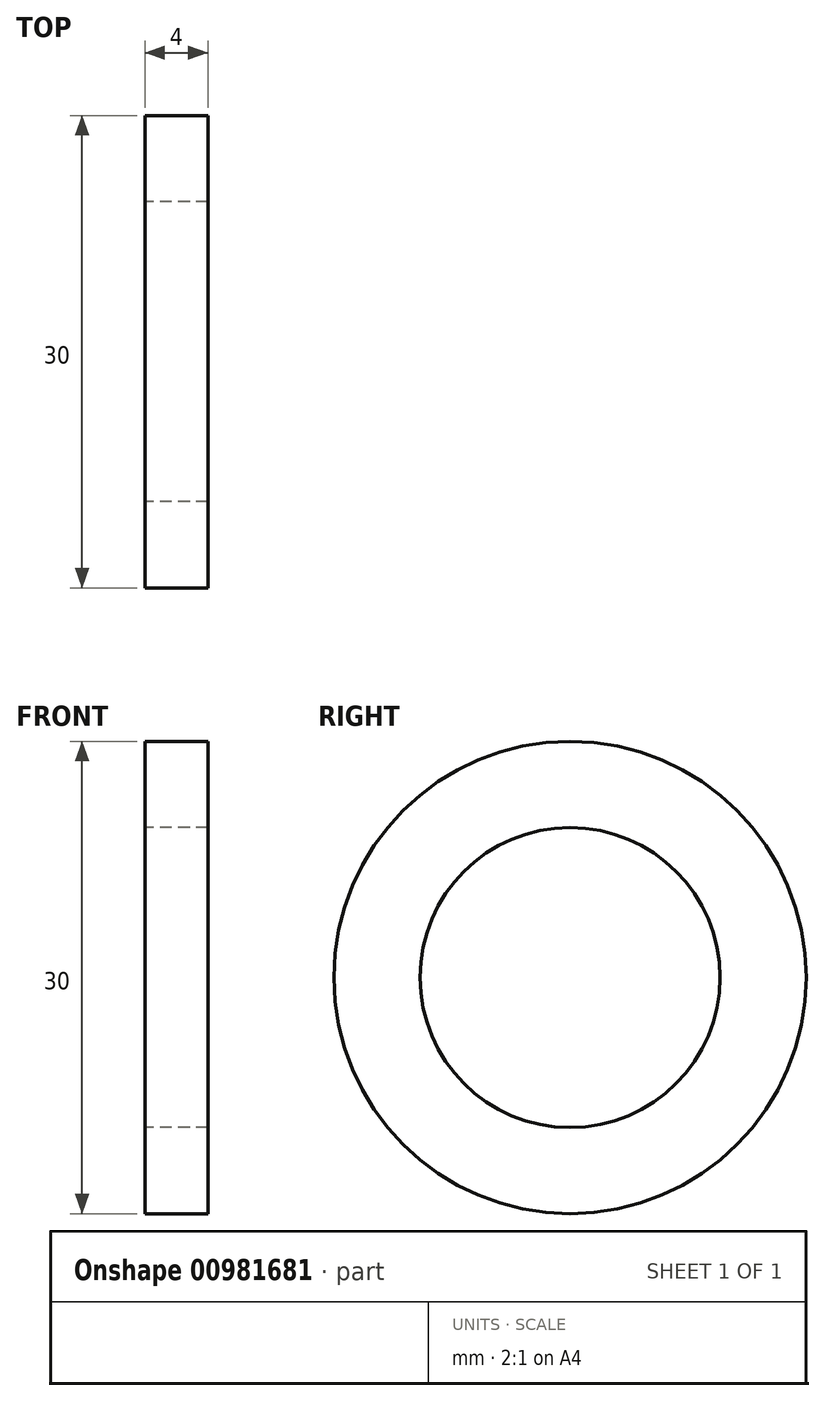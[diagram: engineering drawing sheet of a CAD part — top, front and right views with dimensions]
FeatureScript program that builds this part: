
annotation { "Feature Type Name" : "Feature", "Feature Type Description" : "" }
export const myFeature = defineFeature(function(context is Context, id is Id, definition is map)
    precondition{}
    {
        {
            var Q0;
            Q0=qCreatedBy(makeId("Right.planeOp"),FACE);
            var sketch = newSketch(context, id + "F0", { "sketchPlane" : qUnion([Q0])});
            skCircle(sketch, "E0", {"center": v(0, 0) * mm, "radius": 15 * mm});
            skCircle(sketch, "E1", {"center": v(0, 0) * mm, "radius": 9.53 * mm});
            skSolve(sketch);
        }
        {
            var Q0;
            Q0 = qSketchRegion(id + "F0", true);
            extrude(context, id + "F1", {"entities" : qUnion([Q0]), "depth" : 4 * mm, "offsetDistance" : 25 * mm});
        }
    });
